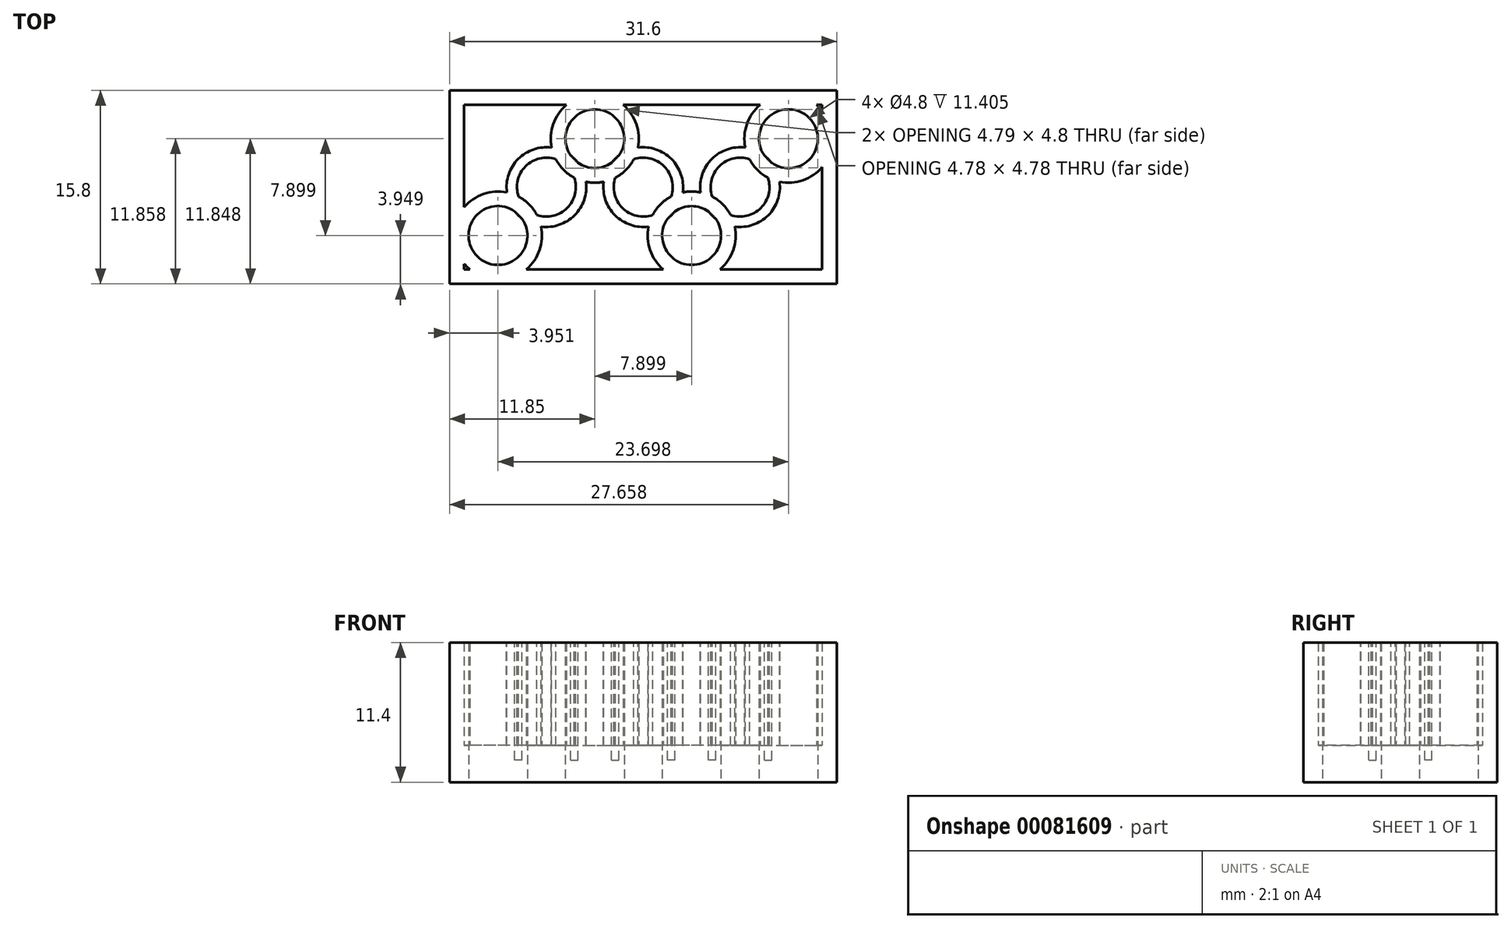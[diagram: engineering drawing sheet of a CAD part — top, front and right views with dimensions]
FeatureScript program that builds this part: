
annotation { "Feature Type Name" : "Feature", "Feature Type Description" : "" }
export const myFeature = defineFeature(function(context is Context, id is Id, definition is map)
    precondition{}
    {
        {
            var Q0;
            Q0=qCreatedBy(makeId("Top.planeOp"),FACE);
            var sketch = newSketch(context, id + "F0", { "sketchPlane" : qUnion([Q0])});
            skLineSegment(sketch, "E0", {"start": v(-11.85, 8.6) * mm, "end": v(-3.95, 8.6) * mm, "construction": true});
            skLineSegment(sketch, "E1", {"start": v(-7.9, 8.6) * mm, "end": v(-7.9, 16.5) * mm, "construction": true});
            skPoint(sketch, "E2.endSnap0", {"position": v(-7.9, 12.55) * mm});
            skLineSegment(sketch, "E3", {"start": v(-3.95, 12.55) * mm, "end": v(-11.85, 12.55) * mm, "construction": true});
            skCircle(sketch, "E4", {"center": v(-7.9, 12.55) * mm, "radius": 2.4 * mm});
            skLineSegment(sketch, "E5", {"start": v(-11.85, 8.6) * mm, "end": v(-11.85, 16.5) * mm});
            skLineSegment(sketch, "E6", {"start": v(-11.85, 16.5) * mm, "end": v(-3.95, 16.5) * mm});
            skLineSegment(sketch, "E7", {"start": v(-3.95, 16.5) * mm, "end": v(-3.95, 8.6) * mm, "construction": true});
            skCircle(sketch, "E8.MirrorC", {"center": v(0, 12.55) * mm, "radius": 2.4 * mm});
            skLineSegment(sketch, "E9.MirrorCS", {"start": v(0, 8.6) * mm, "end": v(0, 16.5) * mm, "construction": true});
            skLineSegment(sketch, "E10.MirrorCS", {"start": v(-3.95, 12.55) * mm, "end": v(3.95, 12.55) * mm, "construction": true});
            skLineSegment(sketch, "E11.MirrorCS", {"start": v(3.95, 8.6) * mm, "end": v(-3.95, 8.6) * mm, "construction": true});
            skLineSegment(sketch, "E12.MirrorCS", {"start": v(3.95, 16.5) * mm, "end": v(-3.95, 16.5) * mm});
            skPoint(sketch, "E13.MirrorP", {"position": v(0, 4.65) * mm});
            skCircle(sketch, "E14.MirrorC", {"center": v(-7.9, 4.65) * mm, "radius": 2.4 * mm});
            skLineSegment(sketch, "E15.MirrorCS", {"start": v(-3.95, 4.65) * mm, "end": v(-11.85, 4.65) * mm, "construction": true});
            skLineSegment(sketch, "E16.MirrorCS", {"start": v(-7.9, 8.6) * mm, "end": v(-7.9, 0.7) * mm, "construction": true});
            skLineSegment(sketch, "E17.MirrorCS", {"start": v(3.95, 0.7) * mm, "end": v(-3.95, 0.7) * mm});
            skCircle(sketch, "E18.MirrorC", {"center": v(0, 4.65) * mm, "radius": 2.4 * mm});
            skLineSegment(sketch, "E19.MirrorCS", {"start": v(-3.95, 4.65) * mm, "end": v(3.95, 4.65) * mm, "construction": true});
            skLineSegment(sketch, "E20.MirrorCS", {"start": v(-11.85, 0.7) * mm, "end": v(-3.95, 0.7) * mm});
            skLineSegment(sketch, "E21.MirrorCS", {"start": v(-11.85, 8.6) * mm, "end": v(-11.85, 0.7) * mm});
            skLineSegment(sketch, "E22.MirrorCS", {"start": v(0, 8.6) * mm, "end": v(0, 0.7) * mm, "construction": true});
            skLineSegment(sketch, "E23.MirrorCS", {"start": v(3.95, 8.6) * mm, "end": v(3.95, 0.7) * mm, "construction": true});
            skLineSegment(sketch, "E24.MirrorCS", {"start": v(-3.95, 0.7) * mm, "end": v(-3.95, 8.6) * mm, "construction": true});
            skLineSegment(sketch, "E25.MirrorCS", {"start": v(3.95, 8.6) * mm, "end": v(3.95, 16.5) * mm, "construction": true});
            skLineSegment(sketch, "E26.MirrorCS", {"start": v(3.95, 16.5) * mm, "end": v(11.85, 16.5) * mm});
            skLineSegment(sketch, "E27.MirrorCS", {"start": v(11.85, 12.55) * mm, "end": v(3.95, 12.55) * mm, "construction": true});
            skLineSegment(sketch, "E28.MirrorCS", {"start": v(3.95, 8.6) * mm, "end": v(11.85, 8.6) * mm, "construction": true});
            skLineSegment(sketch, "E29.MirrorCS", {"start": v(11.85, 4.65) * mm, "end": v(3.95, 4.65) * mm, "construction": true});
            skLineSegment(sketch, "E30.MirrorCS", {"start": v(3.95, 0.7) * mm, "end": v(11.85, 0.7) * mm});
            skLineSegment(sketch, "E31.MirrorCS", {"start": v(19.75, 8.6) * mm, "end": v(11.85, 8.6) * mm, "construction": true});
            skPoint(sketch, "E32.MirrorP", {"position": v(15.8, 4.65) * mm});
            skCircle(sketch, "E33.MirrorC", {"center": v(7.9, 12.55) * mm, "radius": 2.4 * mm});
            skLineSegment(sketch, "E34.MirrorCS", {"start": v(19.75, 8.6) * mm, "end": v(19.75, 16.5) * mm});
            skPoint(sketch, "E35.MirrorP", {"position": v(7.9, 4.65) * mm});
            skLineSegment(sketch, "E36.MirrorCS", {"start": v(15.8, 8.6) * mm, "end": v(15.8, 0.7) * mm, "construction": true});
            skLineSegment(sketch, "E37.MirrorCS", {"start": v(15.8, 8.6) * mm, "end": v(15.8, 16.5) * mm, "construction": true});
            skCircle(sketch, "E38.MirrorC", {"center": v(7.9, 4.65) * mm, "radius": 2.4 * mm});
            skLineSegment(sketch, "E39.MirrorCS", {"start": v(11.85, 4.65) * mm, "end": v(19.75, 4.65) * mm, "construction": true});
            skLineSegment(sketch, "E40.MirrorCS", {"start": v(7.9, 8.6) * mm, "end": v(7.9, 0.7) * mm, "construction": true});
            skCircle(sketch, "E41.MirrorC", {"center": v(15.8, 12.55) * mm, "radius": 2.4 * mm});
            skLineSegment(sketch, "E42.MirrorCS", {"start": v(19.75, 8.6) * mm, "end": v(19.75, 0.7) * mm});
            skLineSegment(sketch, "E43.MirrorCS", {"start": v(11.85, 12.55) * mm, "end": v(19.75, 12.55) * mm, "construction": true});
            skLineSegment(sketch, "E44.MirrorCS", {"start": v(19.75, 16.5) * mm, "end": v(11.85, 16.5) * mm});
            skLineSegment(sketch, "E45.MirrorCS", {"start": v(19.75, 0.7) * mm, "end": v(11.85, 0.7) * mm});
            skLineSegment(sketch, "E46.MirrorCS", {"start": v(7.9, 8.6) * mm, "end": v(7.9, 16.5) * mm, "construction": true});
            skCircle(sketch, "E47.MirrorC", {"center": v(15.8, 4.65) * mm, "radius": 2.4 * mm});
            skLineSegment(sketch, "E48.MirrorCS", {"start": v(11.85, 16.5) * mm, "end": v(11.85, 8.6) * mm, "construction": true});
            skLineSegment(sketch, "E49.MirrorCS", {"start": v(11.85, 0.7) * mm, "end": v(11.85, 8.6) * mm, "construction": true});
            skSolve(sketch);
        }
        {
            var Q0;
            Q0=makeQuery(id+"F0.imprint","IMPRINT",FACE,{"disambiguationData":[TD([[makeQuery(id+"F0.imprint","IMPRINT",EDGE,{"derivedFrom":sQuery(id+"F0.wireOp",EDGE,"E4")}),-1.0]])]});
            var Q1;
            Q1=makeQuery(id+"F0.imprint","IMPRINT",FACE,{"disambiguationData":[TD([[makeQuery(id+"F0.imprint","IMPRINT",EDGE,{"derivedFrom":sQuery(id+"F0.wireOp",EDGE,"E23.MirrorCS")}),1.0]])]});
            var Q2;
            Q2=makeQuery(id+"F0.imprint","IMPRINT",FACE,{"disambiguationData":[TD([[makeQuery(id+"F0.imprint","IMPRINT",EDGE,{"derivedFrom":sQuery(id+"F0.wireOp",EDGE,"fc123e6f-537d-4096-946d-5862537fccc576.MirrorC")}),-1.0]])]});
            var Q3;
            Q3=makeQuery(id+"F0.imprint","IMPRINT",FACE,{"disambiguationData":[TD([[makeQuery(id+"F0.imprint","IMPRINT",EDGE,{"derivedFrom":sQuery(id+"F0.wireOp",EDGE,"fc123e6f-537d-4096-946d-5862537fccc586.MirrorC")}),1.0]])]});
            var Q4;
            Q4=makeQuery(id+"F0.imprint","IMPRINT",FACE,{"disambiguationData":[TD([[makeQuery(id+"F0.imprint","IMPRINT",EDGE,{"derivedFrom":sQuery(id+"F0.wireOp",EDGE,"2a1663f3-ffc9-468e-a9db-4e92d239e64719.MirrorC")}),1.0]])]});
            var Q5;
            Q5=makeQuery(id+"F0.imprint","IMPRINT",FACE,{"disambiguationData":[TD([[makeQuery(id+"F0.imprint","IMPRINT",EDGE,{"derivedFrom":sQuery(id+"F0.wireOp",EDGE,"2a1663f3-ffc9-468e-a9db-4e92d239e64715.MirrorC")}),-1.0]])]});
            var Q6;
            Q6=makeQuery(id+"F0.imprint","IMPRINT",FACE,{"disambiguationData":[TD([[makeQuery(id+"F0.imprint","IMPRINT",EDGE,{"derivedFrom":sQuery(id+"F0.wireOp",EDGE,"E14.MirrorC")}),-1.0]])]});
            var Q7;
            Q7=makeQuery(id+"F0.imprint","IMPRINT",FACE,{"disambiguationData":[TD([[makeQuery(id+"F0.imprint","IMPRINT",EDGE,{"derivedFrom":sQuery(id+"F0.wireOp",EDGE,"E4")}),1.0]])]});
            var Q8;
            Q8=makeQuery(id+"F0.imprint","IMPRINT",FACE,{"disambiguationData":[TD([[makeQuery(id+"F0.imprint","IMPRINT",EDGE,{"derivedFrom":sQuery(id+"F0.wireOp",EDGE,"E18.MirrorC")}),1.0]])]});
            var Q9;
            Q9=makeQuery(id+"F0.imprint","IMPRINT",FACE,{"disambiguationData":[TD([[makeQuery(id+"F0.imprint","IMPRINT",EDGE,{"derivedFrom":sQuery(id+"F0.wireOp",EDGE,"E8.MirrorC")}),-1.0]])]});
            var Q10;
            Q10=makeQuery(id+"F0.imprint","IMPRINT",FACE,{"disambiguationData":[TD([[makeQuery(id+"F0.imprint","IMPRINT",EDGE,{"derivedFrom":sQuery(id+"F0.wireOp",EDGE,"E38.MirrorC")}),-1.0]])]});
            var Q11;
            Q11=makeQuery(id+"F0.imprint","IMPRINT",FACE,{"disambiguationData":[TD([[makeQuery(id+"F0.imprint","IMPRINT",EDGE,{"derivedFrom":sQuery(id+"F0.wireOp",EDGE,"E47.MirrorC")}),1.0]])]});
            var Q12;
            Q12=makeQuery(id+"F0.imprint","IMPRINT",FACE,{"disambiguationData":[TD([[makeQuery(id+"F0.imprint","IMPRINT",EDGE,{"derivedFrom":sQuery(id+"F0.wireOp",EDGE,"E41.MirrorC")}),-1.0]])]});
            var Q13;
            Q13=makeQuery(id+"F0.imprint","IMPRINT",FACE,{"disambiguationData":[TD([[makeQuery(id+"F0.imprint","IMPRINT",EDGE,{"derivedFrom":sQuery(id+"F0.wireOp",EDGE,"E33.MirrorC")}),1.0]])]});
            extrude(context, id + "F1", {"entities" : qUnion([Q0, Q1, Q2, Q3, Q4, Q5, Q6, Q7, Q8, Q9, Q10, Q11, Q12, Q13]), "depth" : 9.6 * mm});
        }
        {
            var Q0;
            Q0=makeQuery(id+"F0.imprint","IMPRINT",FACE,{"disambiguationData":[TD([[makeQuery(id+"F0.imprint","IMPRINT",EDGE,{"derivedFrom":sQuery(id+"F0.wireOp",EDGE,"E14.MirrorC")}),-1.0]])]});
            var Q1;
            Q1=makeQuery(id+"F0.imprint","IMPRINT",FACE,{"disambiguationData":[TD([[makeQuery(id+"F0.imprint","IMPRINT",EDGE,{"derivedFrom":sQuery(id+"F0.wireOp",EDGE,"E18.MirrorC")}),1.0]])]});
            var Q2;
            Q2=makeQuery(id+"F0.imprint","IMPRINT",FACE,{"disambiguationData":[TD([[makeQuery(id+"F0.imprint","IMPRINT",EDGE,{"derivedFrom":sQuery(id+"F0.wireOp",EDGE,"fc123e6f-537d-4096-946d-5862537fccc576.MirrorC")}),-1.0]])]});
            var Q3;
            Q3=makeQuery(id+"F0.imprint","IMPRINT",FACE,{"disambiguationData":[TD([[makeQuery(id+"F0.imprint","IMPRINT",EDGE,{"derivedFrom":sQuery(id+"F0.wireOp",EDGE,"fc123e6f-537d-4096-946d-5862537fccc586.MirrorC")}),1.0]])]});
            var Q4;
            Q4=makeQuery(id+"F0.imprint","IMPRINT",FACE,{"disambiguationData":[TD([[makeQuery(id+"F0.imprint","IMPRINT",EDGE,{"derivedFrom":sQuery(id+"F0.wireOp",EDGE,"E8.MirrorC")}),-1.0]])]});
            var Q5;
            Q5=makeQuery(id+"F0.imprint","IMPRINT",FACE,{"disambiguationData":[TD([[makeQuery(id+"F0.imprint","IMPRINT",EDGE,{"derivedFrom":sQuery(id+"F0.wireOp",EDGE,"E4")}),1.0]])]});
            var Q6;
            Q6=makeQuery(id+"F0.imprint","IMPRINT",FACE,{"disambiguationData":[TD([[makeQuery(id+"F0.imprint","IMPRINT",EDGE,{"derivedFrom":sQuery(id+"F0.wireOp",EDGE,"2a1663f3-ffc9-468e-a9db-4e92d239e64719.MirrorC")}),1.0]])]});
            var Q7;
            Q7=makeQuery(id+"F0.imprint","IMPRINT",FACE,{"disambiguationData":[TD([[makeQuery(id+"F0.imprint","IMPRINT",EDGE,{"derivedFrom":sQuery(id+"F0.wireOp",EDGE,"2a1663f3-ffc9-468e-a9db-4e92d239e64715.MirrorC")}),-1.0]])]});
            var Q8;
            Q8=makeQuery(id+"F0.imprint","IMPRINT",FACE,{"disambiguationData":[TD([[makeQuery(id+"F0.imprint","IMPRINT",EDGE,{"derivedFrom":sQuery(id+"F0.wireOp",EDGE,"E38.MirrorC")}),-1.0]])]});
            var Q9;
            Q9=makeQuery(id+"F0.imprint","IMPRINT",FACE,{"disambiguationData":[TD([[makeQuery(id+"F0.imprint","IMPRINT",EDGE,{"derivedFrom":sQuery(id+"F0.wireOp",EDGE,"E33.MirrorC")}),1.0]])]});
            var Q10;
            Q10=makeQuery(id+"F0.imprint","IMPRINT",FACE,{"disambiguationData":[TD([[makeQuery(id+"F0.imprint","IMPRINT",EDGE,{"derivedFrom":sQuery(id+"F0.wireOp",EDGE,"E47.MirrorC")}),1.0]])]});
            var Q11;
            Q11=makeQuery(id+"F0.imprint","IMPRINT",FACE,{"disambiguationData":[TD([[makeQuery(id+"F0.imprint","IMPRINT",EDGE,{"derivedFrom":sQuery(id+"F0.wireOp",EDGE,"E41.MirrorC")}),-1.0]])]});
            extrude(context, id + "F2", {"entities" : qUnion([Q0, Q1, Q2, Q3, Q4, Q5, Q6, Q7, Q8, Q9, Q10, Q11]), "oppositeDirection" : true, "depth" : 1.8 * mm});
        }
        {
            var Q0;
            Q0=makeQuery(id+"F1.opExtrude","CAP_FACE",FACE,{"disambiguationData":[OSD([sQuery(id+"F0.wireOp",EDGE,"E12.MirrorCS"),sQuery(id+"F0.wireOp",EDGE,"E5"),sQuery(id+"F0.wireOp",EDGE,"E6"),sQuery(id+"F0.wireOp",EDGE,"E17.MirrorCS"),sQuery(id+"F0.wireOp",EDGE,"E20.MirrorCS"),sQuery(id+"F0.wireOp",EDGE,"E21.MirrorCS"),sQuery(id+"F0.wireOp",EDGE,"fc123e6f-537d-4096-946d-5862537fccc577.MirrorCS"),sQuery(id+"F0.wireOp",EDGE,"fc123e6f-537d-4096-946d-5862537fccc589.MirrorCS"),sQuery(id+"F0.wireOp",EDGE,"2a1663f3-ffc9-468e-a9db-4e92d239e64713.MirrorCS"),sQuery(id+"F0.wireOp",EDGE,"2a1663f3-ffc9-468e-a9db-4e92d239e64717.MirrorCS"),sQuery(id+"F0.wireOp",EDGE,"SH8cYdFG-BgHv-yaXF-4xOE-xr2LJAi7gf8K")])],"isStart":false});
            shell(context, id + "F3", {"entities" : qUnion([Q0]), "thickness" : 1.2 * mm});
        }
        {
            var Q0;
            Q0=makeQuery(id+"F1.opExtrude","CAP_FACE",FACE,{"disambiguationData":[OSD([sQuery(id+"F0.wireOp",EDGE,"E12.MirrorCS"),sQuery(id+"F0.wireOp",EDGE,"E5"),sQuery(id+"F0.wireOp",EDGE,"E6"),sQuery(id+"F0.wireOp",EDGE,"E17.MirrorCS"),sQuery(id+"F0.wireOp",EDGE,"E20.MirrorCS"),sQuery(id+"F0.wireOp",EDGE,"E21.MirrorCS"),sQuery(id+"F0.wireOp",EDGE,"fc123e6f-537d-4096-946d-5862537fccc577.MirrorCS"),sQuery(id+"F0.wireOp",EDGE,"fc123e6f-537d-4096-946d-5862537fccc589.MirrorCS"),sQuery(id+"F0.wireOp",EDGE,"XBb4UonK-w9EM-ELhb-oUkg-e4OY1im9nSWL")])],"isStart":false});
            var sketch = newSketch(context, id + "F4", { "sketchPlane" : qUnion([Q0])});
            skLineSegment(sketch, "E50", {"start": v(-11.85, 8.6) * mm, "end": v(-3.95, 8.6) * mm, "construction": true});
            skLineSegment(sketch, "E51", {"start": v(-3.95, 8.6) * mm, "end": v(3.95, 8.6) * mm, "construction": true});
            skCircle(sketch, "E52", {"center": v(-3.95, 8.6) * mm, "radius": 3.25 * mm});
            skCircle(sketch, "E53", {"center": v(3.95, 8.6) * mm, "radius": 3.25 * mm});
            skCircle(sketch, "E54", {"center": v(-3.95, 8.6) * mm, "radius": 2.4 * mm});
            skCircle(sketch, "E55", {"center": v(3.95, 8.6) * mm, "radius": 2.4 * mm});
            skLineSegment(sketch, "E56", {"start": v(3.95, 8.6) * mm, "end": v(11.85, 8.6) * mm, "construction": true});
            skLineSegment(sketch, "E57", {"start": v(3.95, 16.5) * mm, "end": v(3.95, 0.7) * mm, "construction": true});
            skCircle(sketch, "E58", {"center": v(11.85, 8.6) * mm, "radius": 3.25 * mm});
            skCircle(sketch, "E59", {"center": v(11.85, 8.6) * mm, "radius": 2.4 * mm});
            skLineSegment(sketch, "E60", {"start": v(11.85, 8.6) * mm, "end": v(19.75, 8.6) * mm, "construction": true});
            skSolve(sketch);
        }
        {
            var Q0;
            Q0 = qSketchRegion(id + "F4", true);
            extrude(context, id + "F5", {"entities" : qUnion([Q0]), "operationType" : NewBodyOperationType.ADD, "oppositeDirection" : true, "depth" : 9.6 * mm});
        }
    });
